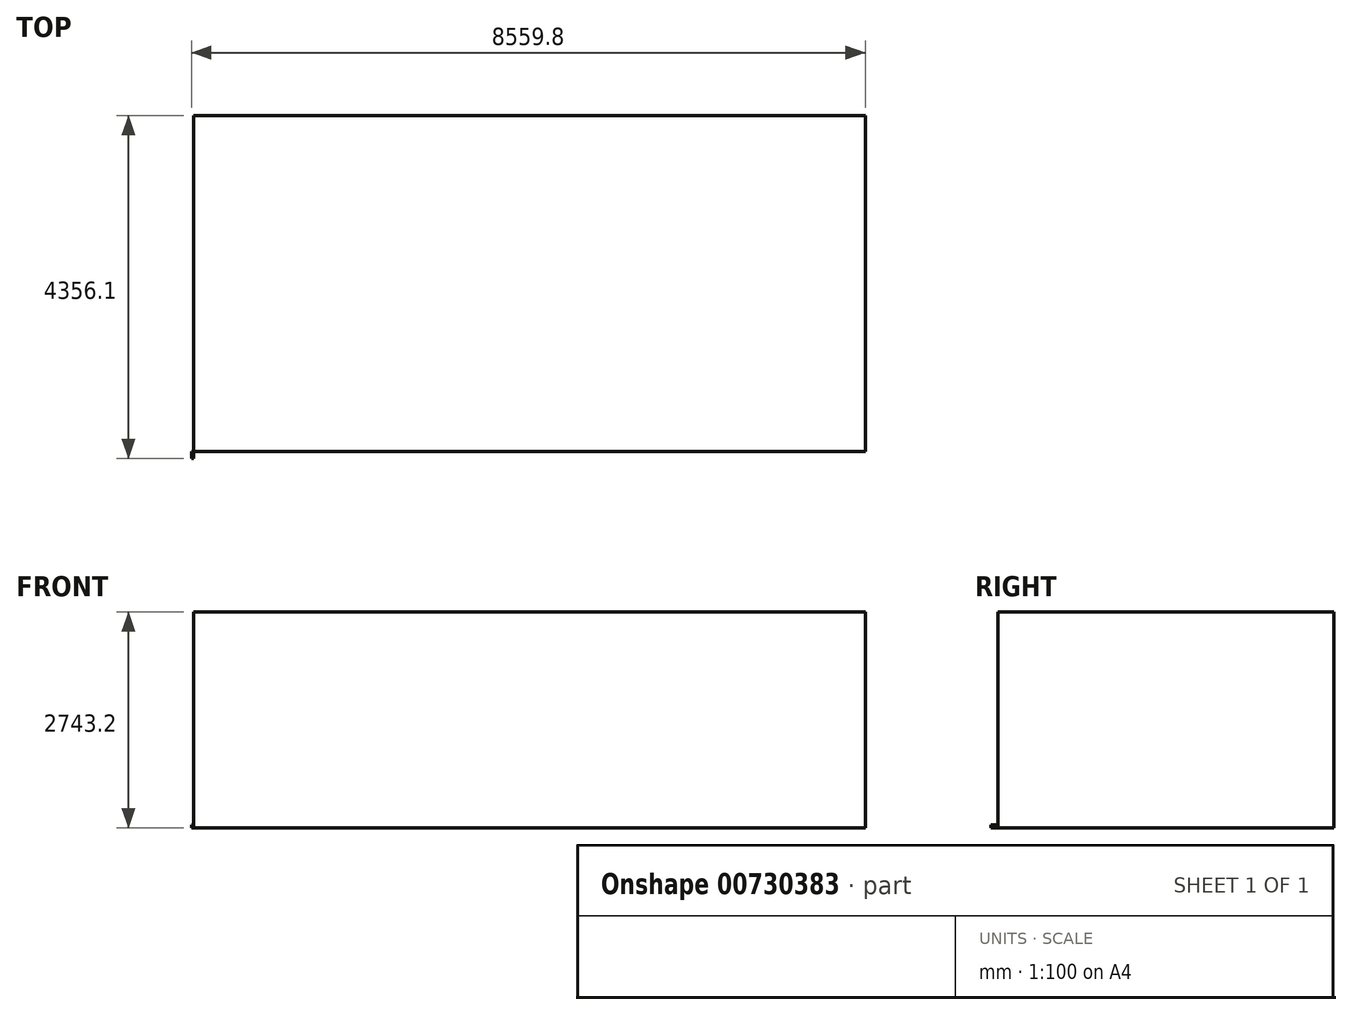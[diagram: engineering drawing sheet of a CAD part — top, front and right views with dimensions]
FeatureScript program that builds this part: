
annotation { "Feature Type Name" : "Feature", "Feature Type Description" : "" }
export const myFeature = defineFeature(function(context is Context, id is Id, definition is map)
    precondition{}
    {
        {
            var Q0;
            Q0=qCreatedBy(makeId("Front.planeOp"),FACE);
            var sketch = newSketch(context, id + "F0", { "sketchPlane" : qUnion([Q0])});
            skLineSegment(sketch, "E0.bottom", {"start": v(0, 0) * mm, "end": v(8534.4, 0) * mm});
            skLineSegment(sketch, "E0.top", {"start": v(0, 2743.2) * mm, "end": v(8534.4, 2743.2) * mm});
            skLineSegment(sketch, "E0.left", {"start": v(0, 0) * mm, "end": v(0, 2743.2) * mm});
            skLineSegment(sketch, "E0.right", {"start": v(8534.4, 0) * mm, "end": v(8534.4, 2743.2) * mm});
            skSolve(sketch);
        }
        {
            var Q0;
            Q0=makeQuery(id+"F0.imprint","IMPRINT",FACE,{"disambiguationData":[TD([[makeQuery(id+"F0.imprint","IMPRINT",EDGE,{"derivedFrom":sQuery(id+"F0.wireOp",EDGE,"E0.bottom")}),1.0]])]});
            extrude(context, id + "F1", {"entities" : qUnion([Q0]), "depth" : 4267.2 * mm, "offsetDistance" : 25.4 * mm});
        }
        {
            var Q0;
            Q0=makeQuery(id+"F1.opExtrude","SWEPT_FACE",FACE,{"disambiguationData":[OSD([sQuery(id+"F0.wireOp",EDGE,"E0.left")])]});
            var sketch = newSketch(context, id + "F2", { "sketchPlane" : qUnion([Q0])});
            skLineSegment(sketch, "E1.bottom", {"start": v(4267.2, 0) * mm, "end": v(4356.1, 0) * mm});
            skLineSegment(sketch, "E1.top", {"start": v(4267.2, 38.1) * mm, "end": v(4356.1, 38.1) * mm});
            skLineSegment(sketch, "E1.left", {"start": v(4267.2, 0) * mm, "end": v(4267.2, 38.1) * mm});
            skLineSegment(sketch, "E1.right", {"start": v(4356.1, 0) * mm, "end": v(4356.1, 38.1) * mm});
            skSolve(sketch);
        }
        {
            var Q0;
            Q0=makeQuery(id+"F2.imprint","IMPRINT",FACE,{"disambiguationData":[TD([[makeQuery(id+"F2.imprint","IMPRINT",EDGE,{"derivedFrom":sQuery(id+"F2.wireOp",EDGE,"E1.bottom")}),1.0]])]});
            extrude(context, id + "F3", {"entities" : qUnion([Q0]), "depth" : 25.4 * mm, "offsetDistance" : 25.4 * mm});
        }
    });
